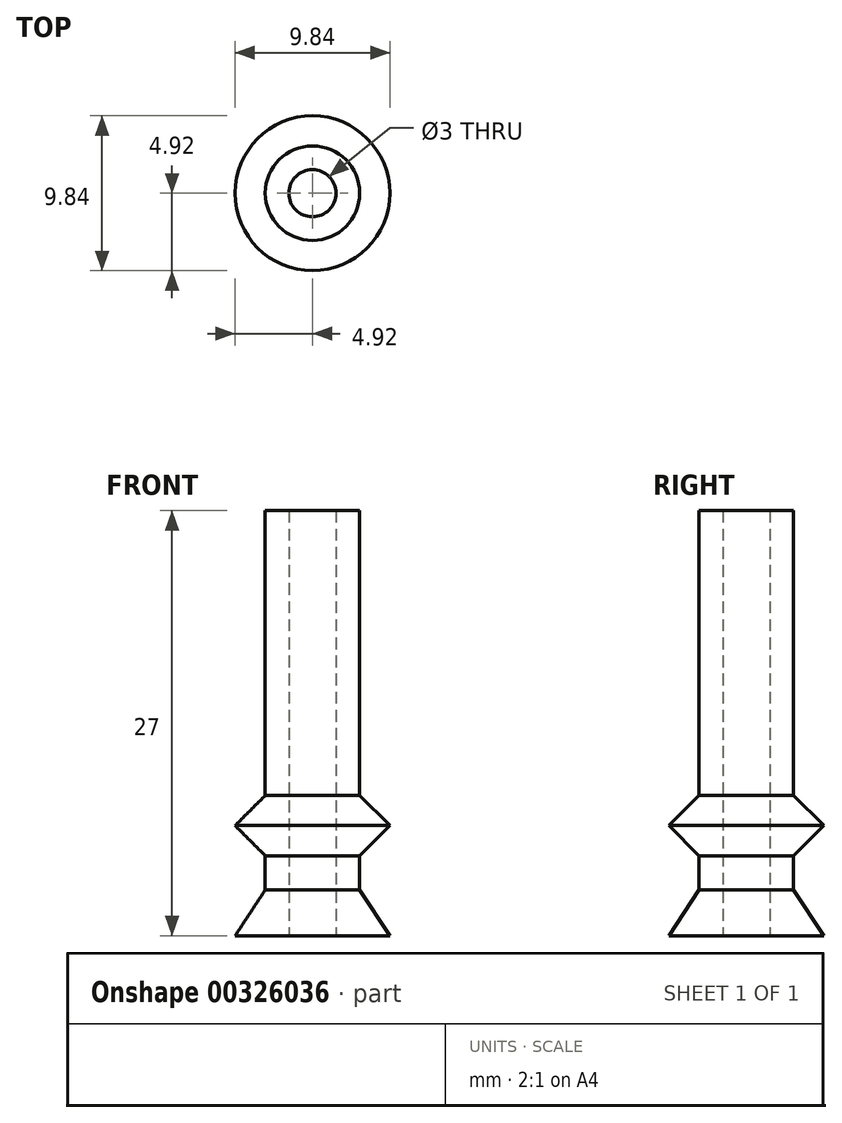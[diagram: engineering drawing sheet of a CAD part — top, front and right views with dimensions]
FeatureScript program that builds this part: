
annotation { "Feature Type Name" : "Feature", "Feature Type Description" : "" }
export const myFeature = defineFeature(function(context is Context, id is Id, definition is map)
    precondition{}
    {
        {
            var Q0;
            Q0=qCreatedBy(makeId("Front.planeOp"),FACE);
            var sketch = newSketch(context, id + "F0", { "sketchPlane" : qUnion([Q0])});
            skLineSegment(sketch, "E0", {"start": v(0, 0) * mm, "end": v(0, 22) * mm, "construction": true});
            skLineSegment(sketch, "E1", {"start": v(0, 22) * mm, "end": v(0, 27) * mm, "construction": true});
            skLineSegment(sketch, "E2", {"start": v(0, 27) * mm, "end": v(1.5, 27) * mm, "construction": true});
            skLineSegment(sketch, "E3", {"start": v(1.5, 27) * mm, "end": v(1.5, 0) * mm});
            skLineSegment(sketch, "E4", {"start": v(4.92, 0) * mm, "end": v(3, 2.93) * mm});
            skLineSegment(sketch, "E5", {"start": v(3, 2.93) * mm, "end": v(3, 27) * mm});
            skLineSegment(sketch, "E6", {"start": v(3, 27) * mm, "end": v(1.5, 27) * mm});
            skLineSegment(sketch, "E7", {"start": v(1.5, 0) * mm, "end": v(4.92, 0) * mm});
            skLineSegment(sketch, "E8", {"start": v(3, 7) * mm, "end": v(4.92, 7) * mm, "construction": true});
            skLineSegment(sketch, "E9", {"start": v(4.92, 7) * mm, "end": v(4.92, 27) * mm, "construction": true});
            skLineSegment(sketch, "E10", {"start": v(4.92, 7) * mm, "end": v(3, 5.08) * mm});
            skLineSegment(sketch, "E11", {"start": v(4.92, 7) * mm, "end": v(3, 8.92) * mm});
            skSolve(sketch);
        }
        {
            var Q0;
            Q0 = qSketchRegion(id + "F0", true);
            var Q1;
            Q1=sQuery(id+"F0.wireOp",EDGE,"E0");
            revolve(context, id + "F1", {"entities" : qUnion([Q0]), "axis" : qUnion([Q1]), "revolveType" : RevolveType.FULL});
        }
    });
